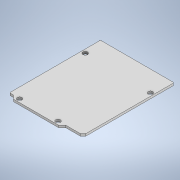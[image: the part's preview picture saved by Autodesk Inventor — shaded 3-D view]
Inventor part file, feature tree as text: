
AUTODESK INVENTOR PART (.ipt)
format: ipt  version: 2021 (Build 250183000, 183)  size: 134,144 bytes
history: native  units: mm
features: chamfer x2, sketch x2, extrude x1, hole x1
ambient origin geometry x8: Origin, YZ Plane, XZ Plane, XY Plane, X Axis, Y Axis, Z Axis, Center Point
bodies: Solid1 (feature_tree)
feature tree (6):
  extrude  "Extrusion1"  Depth=68.75mm
  chamfer  "Chamfer1"  Distance=2.85mm
  chamfer  "Chamfer2"  Distance=2.56mm
  hole  "Hole1"  [1 undecoded]
  sketch  "Sketch1"  dims[d2=53.5mm d12=68.75mm]
  sketch  "Sketch2"  dims[d13=2.6mm d14=2.85mm d15=2.56mm d16=32.86mm d17=12.6mm d18=28.0mm d19=26.0mm d20=1.6mm d21=0.0mm d22=2.0mm d23=2.0mm d24=45.0deg d25=0.5mm d26=2.0mm d27=45.0deg d28=2.7mm d29=13.79mm d30=2.18mm d31=15.0mm d32=7.48mm d33=2.38mm d34=18.0mm d35=3.4mm d36=6.0mm d37=6.3mm d38=2.0mm d39=90.0deg d40=8.0mm d41=20.594885mm]
note: 1 required parameter value undecoded (feature->parameter linkage not recoverable at this tier; creation-order binding heuristic only, values carry confidence <= 0.55)
